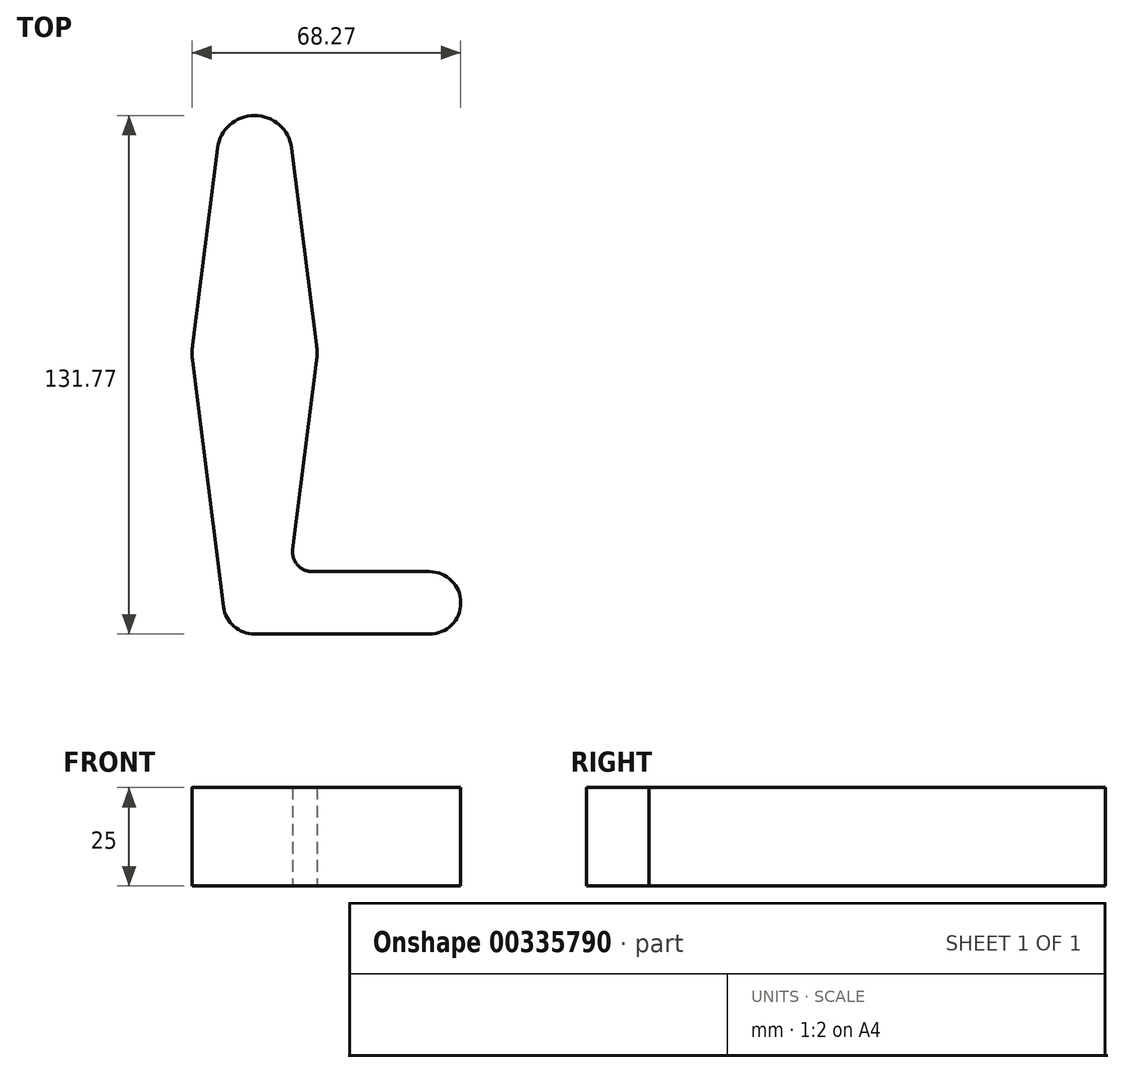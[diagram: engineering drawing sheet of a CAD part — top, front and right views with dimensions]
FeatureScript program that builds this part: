
annotation { "Feature Type Name" : "Feature", "Feature Type Description" : "" }
export const myFeature = defineFeature(function(context is Context, id is Id, definition is map)
    precondition{}
    {
        {
            var Q0;
            Q0=qCreatedBy(makeId("Top.planeOp"),FACE);
            var sketch = newSketch(context, id + "F0", { "sketchPlane" : qUnion([Q0])});
            skLineSegment(sketch, "E0", {"start": v(0, 0) * mm, "end": v(0, 114.3) * mm, "construction": true});
            skCircle(sketch, "E1", {"center": v(0, 0) * mm, "radius": 7.94 * mm});
            skCircle(sketch, "E2", {"center": v(0, 114.3) * mm, "radius": 9.53 * mm});
            skLineSegment(sketch, "E3", {"start": v(0, 0) * mm, "end": v(44.45, 0) * mm, "construction": true});
            skCircle(sketch, "E4", {"center": v(44.45, 0) * mm, "radius": 7.94 * mm});
            skCircle(sketch, "E5", {"center": v(0, 63.5) * mm, "radius": 15.88 * mm});
            skLineSegment(sketch, "E6", {"start": v(-9.45, 115.5) * mm, "end": v(-15.75, 65.48) * mm});
            skLineSegment(sketch, "E7", {"start": v(9.45, 115.5) * mm, "end": v(15.75, 65.48) * mm});
            skLineSegment(sketch, "E8", {"start": v(-15.75, 61.52) * mm, "end": v(-7.88, -1) * mm});
            skLineSegment(sketch, "E9", {"start": v(15.75, 61.52) * mm, "end": v(9.7, 13.56) * mm});
            skLineSegment(sketch, "E10", {"start": v(14.67, 7.94) * mm, "end": v(44.45, 7.94) * mm});
            skLineSegment(sketch, "E11", {"start": v(0, -7.94) * mm, "end": v(44.45, -7.94) * mm});
            skPoint(sketch, "E12.newPointB", {"position": v(0, 7.94) * mm});
            skArc(sketch, "E12.filletArc", {"start": v(9.7, 13.56) * mm, "mid": v(10.92, 9.63) * mm, "end": v(14.67, 7.94) * mm});
            skSolve(sketch);
        }
        {
            var Q0;
            {var subQ0=sQuery(id+"F0.wireOp",EDGE,"E1");var subQ1=makeQuery(id+"F0.imprint","INTERSECT",VERTEX,{"derivedFrom":[subQ0,sQuery(id+"F0.wireOp",EDGE,"E8")]});Q0=makeQuery(id+"F0.imprint","IMPRINT",FACE,{"disambiguationData":[TD([[makeQuery(id+"F0.imprint","IMPRINT",EDGE,{"disambiguationData":[TD([[subQ1,-1.0]])],"derivedFrom":subQ0}),1.0]])]});}
            var Q1;
            {var subQ0=sQuery(id+"F0.wireOp",EDGE,"E4");var subQ1=makeQuery(id+"F0.imprint","INTERSECT",VERTEX,{"derivedFrom":[subQ0,sQuery(id+"F0.wireOp",EDGE,"E10")]});Q1=makeQuery(id+"F0.imprint","IMPRINT",FACE,{"disambiguationData":[TD([[makeQuery(id+"F0.imprint","IMPRINT",EDGE,{"disambiguationData":[TD([[subQ1,-1.0]])],"derivedFrom":subQ0}),1.0]])]});}
            var Q2;
            {var subQ0=sQuery(id+"F0.wireOp",EDGE,"E5");var subQ1=makeQuery(id+"F0.imprint","INTERSECT",VERTEX,{"derivedFrom":[subQ0,sQuery(id+"F0.wireOp",EDGE,"E6")]});Q2=makeQuery(id+"F0.imprint","IMPRINT",FACE,{"disambiguationData":[TD([[makeQuery(id+"F0.imprint","IMPRINT",EDGE,{"disambiguationData":[TD([[subQ1,1.0]])],"derivedFrom":subQ0}),1.0]])]});}
            var Q3;
            {var subQ0=sQuery(id+"F0.wireOp",EDGE,"E8");Q3=makeQuery(id+"F0.imprint","IMPRINT",FACE,{"disambiguationData":[TD([[makeQuery(id+"F0.imprint","IMPRINT",EDGE,{"derivedFrom":subQ0}),1.0]])]});}
            var Q4;
            {var subQ0=sQuery(id+"F0.wireOp",EDGE,"E6");Q4=makeQuery(id+"F0.imprint","IMPRINT",FACE,{"disambiguationData":[TD([[makeQuery(id+"F0.imprint","IMPRINT",EDGE,{"derivedFrom":subQ0}),1.0]])]});}
            var Q5;
            {var subQ0=sQuery(id+"F0.wireOp",EDGE,"E2");var subQ1=makeQuery(id+"F0.imprint","INTERSECT",VERTEX,{"derivedFrom":[subQ0,sQuery(id+"F0.wireOp",EDGE,"E6")]});Q5=makeQuery(id+"F0.imprint","IMPRINT",FACE,{"disambiguationData":[TD([[makeQuery(id+"F0.imprint","IMPRINT",EDGE,{"disambiguationData":[TD([[subQ1,1.0]])],"derivedFrom":subQ0}),1.0]])]});}
            extrude(context, id + "F1", {"entities" : qUnion([Q0, Q1, Q2, Q3, Q4, Q5]), "depth" : 25 * mm});
        }
    });
